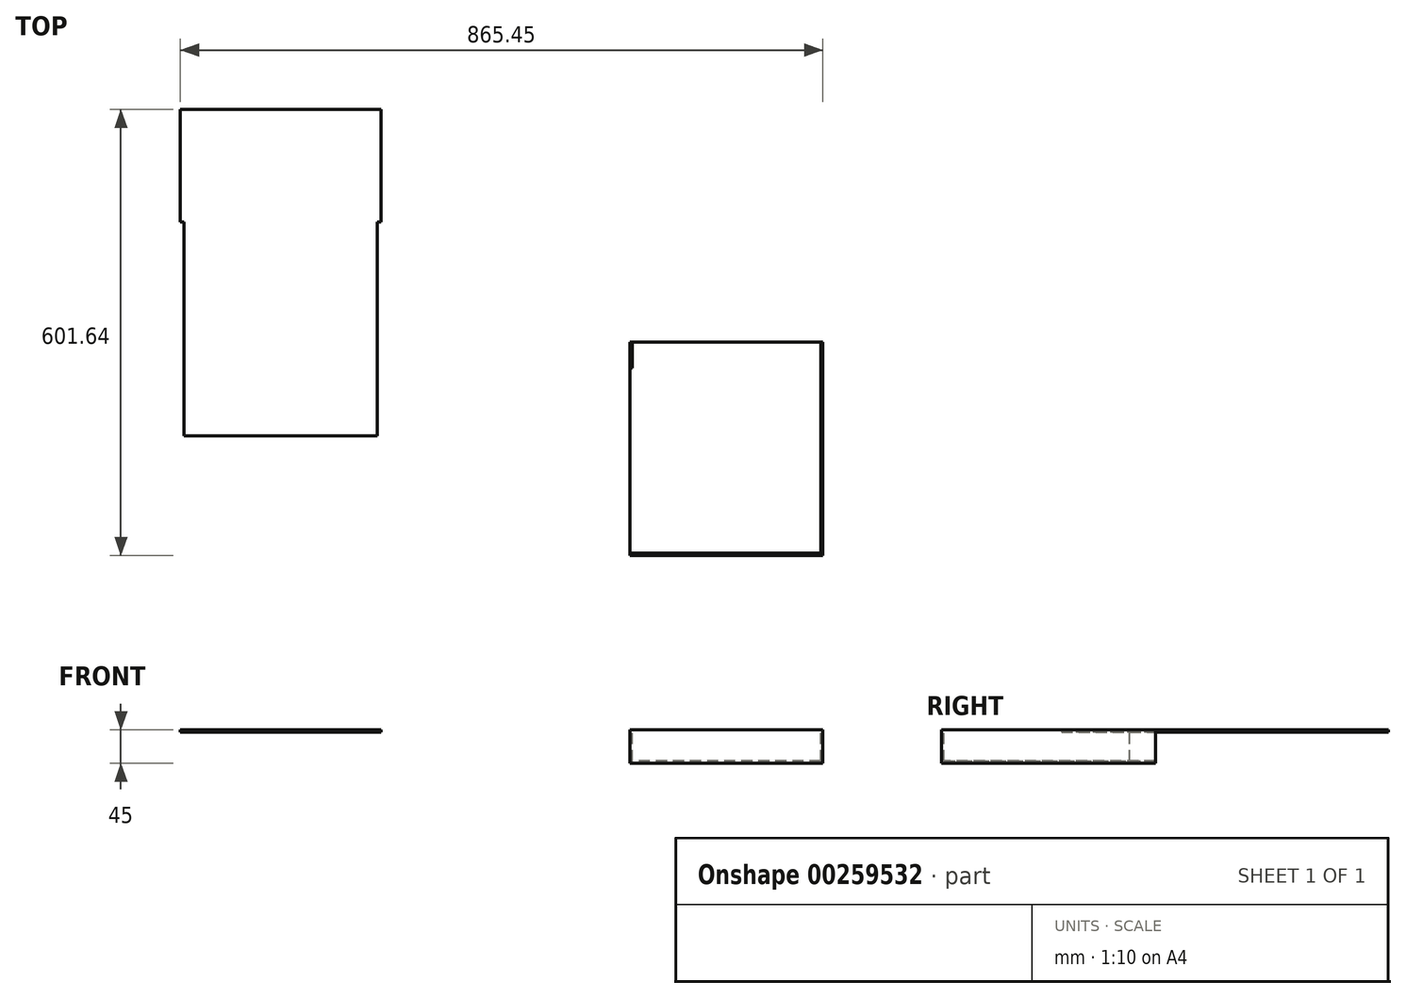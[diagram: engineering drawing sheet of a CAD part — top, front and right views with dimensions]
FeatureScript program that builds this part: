
annotation { "Feature Type Name" : "Feature", "Feature Type Description" : "" }
export const myFeature = defineFeature(function(context is Context, id is Id, definition is map)
    precondition{}
    {
        {
            var Q0;
            Q0=qCreatedBy(makeId("Top.planeOp"),FACE);
            var sketch = newSketch(context, id + "F0", { "sketchPlane" : qUnion([Q0])});
            skLineSegment(sketch, "E0", {"start": v(-83.1, 208.4) * mm, "end": v(186.9, 208.4) * mm});
            skLineSegment(sketch, "E1", {"start": v(186.9, 208.4) * mm, "end": v(186.9, 56.4) * mm});
            skLineSegment(sketch, "E2", {"start": v(186.9, 56.4) * mm, "end": v(181.9, 56.4) * mm});
            skLineSegment(sketch, "E3", {"start": v(181.9, 56.4) * mm, "end": v(181.9, -231.6) * mm});
            skLineSegment(sketch, "E4", {"start": v(181.9, -231.6) * mm, "end": v(-78.1, -231.6) * mm});
            skLineSegment(sketch, "E5", {"start": v(-78.1, -231.6) * mm, "end": v(-78.1, 56.4) * mm});
            skLineSegment(sketch, "E6", {"start": v(-78.1, 56.4) * mm, "end": v(-83.1, 56.4) * mm});
            skLineSegment(sketch, "E7", {"start": v(-83.1, 56.4) * mm, "end": v(-83.1, 208.4) * mm});
            skSolve(sketch);
        }
        {
            var Q0;
            Q0=makeQuery(id+"F0.imprint","IMPRINT",FACE,{"disambiguationData":[TD([[makeQuery(id+"F0.imprint","IMPRINT",EDGE,{"derivedFrom":sQuery(id+"F0.wireOp",EDGE,"E0")}),-1.0]])]});
            extrude(context, id + "F1", {"entities" : qUnion([Q0]), "depth" : 3 * mm});
        }
        {
            var Q0;
            Q0=makeQuery(id+"F1.opExtrude","CAP_FACE",FACE,{"disambiguationData":[OSD([sQuery(id+"F0.wireOp",EDGE,"E0"),sQuery(id+"F0.wireOp",EDGE,"E1"),sQuery(id+"F0.wireOp",EDGE,"E2"),sQuery(id+"F0.wireOp",EDGE,"E3"),sQuery(id+"F0.wireOp",EDGE,"E4"),sQuery(id+"F0.wireOp",EDGE,"E5"),sQuery(id+"F0.wireOp",EDGE,"E6"),sQuery(id+"F0.wireOp",EDGE,"E7")])],"isStart":false});
            var sketch = newSketch(context, id + "F2", { "sketchPlane" : qUnion([Q0])});
            skLineSegment(sketch, "E8.bottom", {"start": v(262.35, 182.76) * mm, "end": v(522.35, 182.76) * mm});
            skLineSegment(sketch, "E8.top", {"start": v(262.35, -105.24) * mm, "end": v(522.35, -105.24) * mm});
            skLineSegment(sketch, "E8.left", {"start": v(262.35, 182.76) * mm, "end": v(262.35, -105.24) * mm});
            skLineSegment(sketch, "E8.right", {"start": v(522.35, 182.76) * mm, "end": v(522.35, -105.24) * mm});
            skSolve(sketch);
        }
        {
            var Q0;
            Q0=makeQuery(id+"F2.imprint","IMPRINT",FACE,{"disambiguationData":[TD([[makeQuery(id+"F2.imprint","IMPRINT",EDGE,{"derivedFrom":sQuery(id+"F2.wireOp",EDGE,"E8.bottom")}),-1.0]])]});
            extrude(context, id + "F3", {"entities" : qUnion([Q0]), "oppositeDirection" : true, "depth" : 45 * mm});
        }
        {
            var Q0;
            Q0=makeQuery(id+"F3.opExtrude","CAP_FACE",FACE,{"disambiguationData":[OSD([sQuery(id+"F2.wireOp",EDGE,"E8.bottom"),sQuery(id+"F2.wireOp",EDGE,"E8.top"),sQuery(id+"F2.wireOp",EDGE,"E8.left"),sQuery(id+"F2.wireOp",EDGE,"E8.right")])],"isStart":true});
            var sketch = newSketch(context, id + "F4", { "sketchPlane" : qUnion([Q0])});
            skLineSegment(sketch, "E9", {"start": v(265.35, -105.24) * mm, "end": v(265.35, 179.76) * mm});
            skLineSegment(sketch, "E10", {"start": v(265.35, 179.76) * mm, "end": v(519.35, 179.76) * mm});
            skLineSegment(sketch, "E11", {"start": v(519.35, 179.76) * mm, "end": v(519.35, -105.24) * mm});
            skSolve(sketch);
        }
        {
            var Q0;
            {var subQ0=sQuery(id+"F4.wireOp",EDGE,"E9");Q0=makeQuery(id+"F4.imprint","IMPRINT",FACE,{"disambiguationData":[TD([[makeQuery(id+"F4.imprint","IMPRINT",EDGE,{"derivedFrom":subQ0}),-1.0]])]});}
            extrude(context, id + "F5", {"entities" : qUnion([Q0]), "operationType" : NewBodyOperationType.REMOVE, "oppositeDirection" : true, "depth" : 42 * mm});
        }
        {
            var Q0;
            Q0=makeQuery(id+"F3.opExtrude","SWEPT_BODY",BODY,{"disambiguationData":[OSD([sQuery(id+"F2.wireOp",EDGE,"E8.bottom"),sQuery(id+"F2.wireOp",EDGE,"E8.top"),sQuery(id+"F2.wireOp",EDGE,"E8.left"),sQuery(id+"F2.wireOp",EDGE,"E8.right")])]});
            var Q1;
            Q1=makeQuery(id+"F3.opExtrude","SWEPT_EDGE",EDGE,{"disambiguationData":[OSD([sQuery(id+"F2.wireOp",EDGE,"E8.top"),sQuery(id+"F2.wireOp",EDGE,"E8.right")])]});
            transform(context, id + "F6", {"entities" : qUnion([Q0]), "transformType" : TransformType.ROTATION, "transformAxis" : qUnion([Q1]), "angle" : 180 * degree, "makeCopy" : false});
        }
        {
            var Q0;
            Q0=makeQuery(id+"F3.opExtrude","CAP_FACE",FACE,{"disambiguationData":[OSD([sQuery(id+"F2.wireOp",EDGE,"E8.bottom"),sQuery(id+"F2.wireOp",EDGE,"E8.top"),sQuery(id+"F2.wireOp",EDGE,"E8.left"),sQuery(id+"F2.wireOp",EDGE,"E8.right")])],"isStart":true});
            var sketch = newSketch(context, id + "F7", { "sketchPlane" : qUnion([Q0])});
            skLineSegment(sketch, "E12", {"start": v(525.35, -390.24) * mm, "end": v(522.35, -390.24) * mm});
            skLineSegment(sketch, "E13", {"start": v(522.35, -390.24) * mm, "end": v(522.35, -140.24) * mm});
            skLineSegment(sketch, "E14", {"start": v(522.35, -140.24) * mm, "end": v(525.35, -140.24) * mm});
            skLineSegment(sketch, "E15", {"start": v(525.35, -140.24) * mm, "end": v(525.35, -390.24) * mm});
            skSolve(sketch);
        }
        {
            var Q0;
            Q0=makeQuery(id+"F7.imprint","IMPRINT",FACE,{"disambiguationData":[TD([[makeQuery(id+"F7.imprint","IMPRINT",EDGE,{"derivedFrom":sQuery(id+"F7.wireOp",EDGE,"E12")}),-1.0]])]});
            extrude(context, id + "F8", {"entities" : qUnion([Q0]), "operationType" : NewBodyOperationType.REMOVE, "oppositeDirection" : true, "depth" : 42 * mm});
        }
    });
